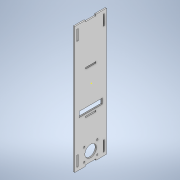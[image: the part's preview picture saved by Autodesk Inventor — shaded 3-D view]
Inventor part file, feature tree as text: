
AUTODESK INVENTOR PART (.ipt)
format: ipt  version: 2020 (Build 240168000, 168)  size: 231,424 bytes
history: native  units: in
note: dims shown in document units (in); Inventor stores cm internally (conversion verified against a paired STEP export)
features: sketch x10, extrude x9
ambient origin geometry x8: Origin, YZ Plane, XZ Plane, XY Plane, X Axis, Y Axis, Z Axis, Center Point
bodies: Solid1 (feature_tree)
feature tree (19):
  extrude  "Extrusion1"  Depth=0.1181in TaperAngle=0.0deg
  extrude  "Extrusion2"  Depth=0.1181in
  extrude  "Extrusion3"  Depth=0.1181in
  extrude  "Extrusion4"  Depth=0.1181in
  extrude  "Extrusion5"  Depth=0.1181in
  extrude  "Extrusion6"  Depth=0.1181in
  sketch  "Sketch7"  dims[d47=0.3937in d48=0.1181in]
  extrude  "Extrusion7"  Depth=0.1181in
  extrude  "Extrusion8"  Depth=0.3937in
  extrude  "Extrusion9"  Depth=1.1811in TaperAngle=0.0deg
  sketch  "Sketch1"  dims[d1=11.811in d9=0.1181in d10=0.0in]
  sketch  "Sketch2"  dims[d22=0.1181in d23=0.0in d29=0.1181in]
  sketch  "Sketch3"  dims[d30=0.1181in d31=0.1181in]
  sketch  "Sketch4"  dims[d32=0.1181in d33=0.9449in]
  sketch  "Sketch5"  dims[d34=0.1181in d35=0.0in d38=0.1181in]
  sketch  "Sketch6"  dims[d39=0.3937in d46=0.1181in]
  sketch  "Sketch8"  dims[d49=0.3937in d50=0.3937in]
  sketch  "Sketch9"  dims[d51=0.1181in d52=1.1811in d53=0.0in]
  sketch  "Sketch10"  dims[d59=0.3937in d60=0.0in d62=0.5906in d63=0.5906in d64=0.3937in d65=0.0in d66=0.1181in d67=0.0in d75=0.1575in d76=0.1575in d77=0.1575in d78=0.1575in d79=0.9449in d80=0.1181in d81=0.0in d82=1.0827in d83=0.3937in d84=0.0in d85=0.1969in d86=0.0344in]
